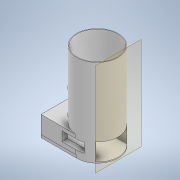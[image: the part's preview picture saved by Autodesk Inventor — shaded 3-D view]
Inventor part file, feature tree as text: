
AUTODESK INVENTOR PART (.ipt)
format: ipt  version: 2021 (Build 250183000, 183)  size: 395,776 bytes
history: native  units: in
note: dims shown in document units (in); Inventor stores cm internally (conversion verified against a paired STEP export)
features: sketch x15, extrude x11, plane x1
ambient origin geometry x8: Origin, YZ Plane, XZ Plane, XY Plane, X Axis, Y Axis, Z Axis, Center Point
bodies: Solid1 (feature_tree)
feature tree (27):
  extrude  "Extrusion1"  Depth=5.0in TaperAngle=0.0deg
  extrude  "Extrusion2"  Depth=5.0in TaperAngle=0.0deg
  extrude  "Extrusion3"  Depth=2.65in TaperAngle=0.0deg
  extrude  "Extrusion4"  Depth=1.1in
  plane  "Work Plane1"
  extrude  "Extrusion5"  Depth=1.175in
  extrude  "Extrusion6"  Depth=1.6in
  sketch  "Sketch7"  dims[d17=0.7in d18=4.0375in d19=0.0in]
  sketch  "Sketch8"  dims[d20=0.7in d21=0.9in]
  sketch  "Sketch9"  dims[d22=4.0375in d23=0.0in d24=2.3in]
  extrude  "Extrusion7"  Depth=0.7in TaperAngle=0.0deg
  extrude  "Extrusion8"  Depth=0.9in
  sketch  "Sketch12"  dims[d29=0.2in]
  extrude  "Extrusion9"  Depth=2.3in
  extrude  "Extrusion10"  Depth=1.0in
  extrude  "Extrusion11"  Depth=0.1in
  sketch  "Sketch1"  dims[d0=3.1in d1=5.0in d2=0.0in]
  sketch  "Sketch2"  dims[d3=3.0in d4=5.0in d5=0.0in]
  sketch  "Sketch3"  dims[d6=1.3in d7=0.0in d8=2.65in d9=0.0in]
  sketch  "Sketch4"  dims[d10=1.1in d11=1.15in]
  sketch  "Sketch5"  dims[d12=1.1in d13=1.175in]
  sketch  "Sketch6"  dims[d14=4.0875in d15=0.0in d16=1.6in]
  sketch  "Sketch10"  dims[d25=1.0in d26=1.0in]
  sketch  "Sketch11"  dims[d27=0.2in d28=0.1in]
  sketch  "Sketch13"  dims[d30=0.1in]
  sketch  "Sketch14"  dims[d31=0.2in]
  sketch  "Sketch15"  dims[d32=0.1in d33=3.275in d34=0.0in d35=3.1in d36=0.2in d37=0.0in d38=0.2in d39=0.0in d40=0.2in d41=2.325in d42=4.1in d43=0.0in]
